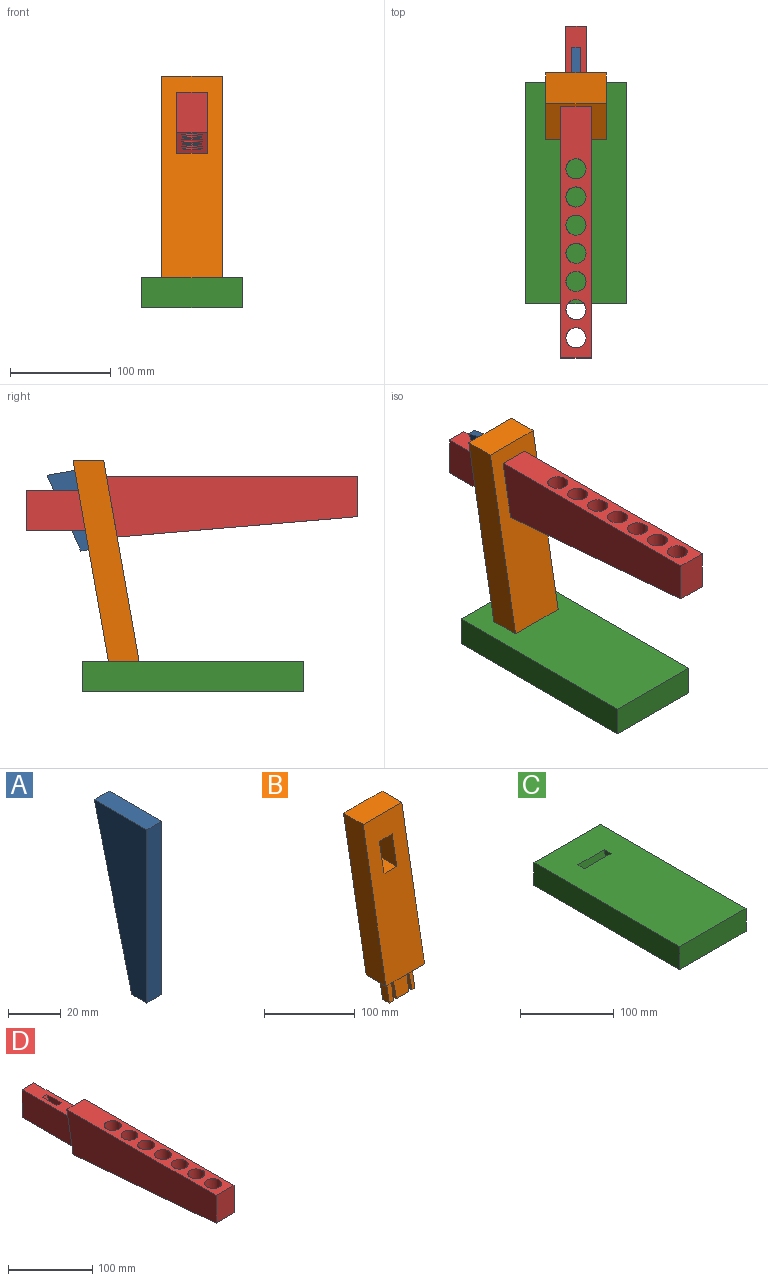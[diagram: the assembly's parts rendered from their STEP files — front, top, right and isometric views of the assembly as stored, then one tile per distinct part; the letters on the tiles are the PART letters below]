
ASSEMBLY  parts=4 mates=3
PART A: 6 faces, bbox 8x28x80 mm
  f0: plane 28x8mm, normal (0,0,1), area 224mm2, adj f1,f3,f4,f5
  f1: plane 80x8mm, normal (0,-1,0), area 640mm2, adj f0,f2,f4,f5
  f2: plane 8x8mm, normal (0,0,-1), area 64mm2, adj f1,f3,f4,f5
  f3: plane 80x20mm, normal (0,0.97,-0.24), area 659.7mm2, adj f0,f2,f4,f5
  f4: plane 80x28mm, normal (-1,0,0), area 1440mm2, adj f0,f1,f2,f3
  f5: plane 80x28mm, normal (1,0,0), area 1440mm2, adj f0,f1,f2,f3
PART B: 25 faces, bbox 60x65.7x230 mm
  f0: plane 30x8mm, normal (0,-0.98,0.17), area 220.9mm2, adj f8,f11,f20,f24
  f1: plane 30x22mm, normal (0,-0.98,0.17), area 624.5mm2, adj f3,f11,f22,f23
  f2: plane 30x6mm, normal (0,-0.98,0.17), area 159.9mm2, adj f4,f11,f19,f21
  f3: plane 19x10.15mm, normal (0,0,-1), area 192.9mm2, adj f1,f6,f22,f23
  f4: plane 10.15x4.5mm, normal (0,0,-1), area 45.7mm2, adj f2,f7,f19,f21
  f5: plane 30x8mm, normal (0,0.98,-0.17), area 220.9mm2, adj f8,f11,f20,f24
  f6: plane 30x22mm, normal (0,0.98,-0.17), area 624.5mm2, adj f3,f11,f22,f23
  f7: plane 30x6mm, normal (0,0.98,-0.17), area 159.9mm2, adj f4,f11,f19,f21
  f8: plane 10.15x6.5mm, normal (0,0,-1), area 66mm2, adj f0,f5,f20,f24
  f9: plane 200x65.73mm, normal (1,0,0), area 6092.6mm2, adj f10,f11,f12,f13
  f10: plane 200x60mm, normal (0,-0.98,0.17), area 11372.8mm2, adj f9,f11,f13,f14,f15,f16,f17,f18
  f11: plane 60x30.46mm, normal (0,0,-1), area 1462.2mm2, adj f0,f1,f2,f5,f6,f7,f9,f10
  f12: plane 200x60mm, normal (0,0.98,-0.17), area 11372.8mm2, adj f9,f11,f13,f14,f15,f16,f17,f18
  f13: plane 60x30.46mm, normal (0,0,1), area 1827.8mm2, adj f9,f10,f12,f14
  f14: plane 200x65.73mm, normal (-1,0,0), area 6092.6mm2, adj f10,f11,f12,f13
  f15: plane 30.46x20mm, normal (0,0,1), area 609.3mm2, adj f10,f12,f16,f18
  f16: plane 40x37.52mm, normal (1,0,0), area 1218.5mm2, adj f10,f12,f15,f17
  f17: plane 30.46x20mm, normal (0,0,-1), area 609.3mm2, adj f10,f12,f16,f18
  f18: plane 40x37.52mm, normal (-1,0,0), area 1218.5mm2, adj f10,f12,f15,f17
  f19: plane 30x15.44mm, normal (1,0,0), area 304.6mm2, adj f2,f4,f7,f11
  f20: plane 30x15.44mm, normal (-1,0,0), area 304.6mm2, adj f0,f5,f8,f11
  f21: plane 30x15.44mm, normal (-1,0,-0.05), area 305mm2, adj f2,f4,f7,f11
  f22: plane 30x15.44mm, normal (1,0,-0.05), area 305mm2, adj f1,f3,f6,f11
  f23: plane 30x15.44mm, normal (-1,0,-0.05), area 305mm2, adj f1,f3,f6,f11
  f24: plane 30x15.44mm, normal (1,0,-0.05), area 305mm2, adj f0,f5,f8,f11
PART C: 10 faces, bbox 100x220x30 mm
  f0: plane 100x30mm, normal (0,1,0), area 3000mm2, adj f1,f3,f4,f5
  f1: plane 220x100mm, normal (0,0,1), area 21593.8mm2, adj f0,f2,f4,f5,f6,f7,f8,f9
  f2: plane 100x30mm, normal (0,-1,0), area 3000mm2, adj f1,f3,f4,f5
  f3: plane 220x100mm, normal (0,0,-1), area 21593.8mm2, adj f0,f2,f4,f5,f6,f7,f8,f9
  f4: plane 220x30mm, normal (-1,0,0), area 6600mm2, adj f0,f1,f2,f3
  f5: plane 220x30mm, normal (1,0,0), area 6600mm2, adj f0,f1,f2,f3
  f6: plane 40x30mm, normal (0,-0.98,0.17), area 1218.5mm2, adj f1,f3,f7,f9
  f7: plane 30x15.44mm, normal (-1,0,0), area 304.6mm2, adj f1,f3,f6,f8
  f8: plane 40x30mm, normal (0,0.98,-0.17), area 1218.5mm2, adj f1,f3,f7,f9
  f9: plane 30x15.44mm, normal (1,0,0), area 304.6mm2, adj f1,f3,f6,f8
PART D: 22 faces, bbox 30.4x330.4x60.6 mm
  f0: plane 89.52x20mm, normal (0,0,-1), area 1681.3mm2, adj f1,f6,f9,f10,f18,f19,f20,f21
  f1: plane 40x20mm, normal (0,1,0), area 800mm2, adj f0,f2,f9,f10
  f2: plane 82.47x20mm, normal (0,0,1), area 1453.9mm2, adj f1,f6,f9,f10,f18,f19,f20,f21
  f3: plane 250x30mm, normal (0,0,1), area 5300.9mm2, adj f4,f6,f7,f8,f11,f12,f13,f14
  f4: plane 40x30mm, normal (0,-1,0), area 1200mm2, adj f3,f5,f7,f8
  f5: plane 239.73x30.36mm, normal (0,-0.08,-1), area 4999.8mm2, adj f4,f6,f7,f8,f11,f12,f13,f14
  f6: plane 60.29x30mm, normal (0,0.98,-0.17), area 1024.2mm2, adj f0,f2,f3,f5,f7,f8,f9,f10
  f7: plane 250x60.29mm, normal (1,0,0), area 12323.4mm2, adj f3,f4,f5,f6
  f8: plane 250x60.29mm, normal (-1,0,0), area 12323.4mm2, adj f3,f4,f5,f6
  f9: plane 89.52x40mm, normal (1,0,0), area 3439.8mm2, adj f0,f1,f2,f6
  f10: plane 89.52x40mm, normal (-1,0,0), area 3439.8mm2, adj f0,f1,f2,f6
  f11: cylinder r=10mm len=56.79mm, axis (0,0,1), area 3516.3mm2, adj f3,f5
  f12: cylinder r=10mm len=54.41mm, axis (0,0,1), area 3367.2mm2, adj f3,f5
  f13: cylinder r=10mm len=52.04mm, axis (0,0,1), area 3218mm2, adj f3,f5
  f14: cylinder r=10mm len=49.67mm, axis (0,0,1), area 3068.9mm2, adj f3,f5
  f15: cylinder r=10mm len=47.29mm, axis (0,0,1), area 2919.8mm2, adj f3,f5
  f16: cylinder r=10mm len=44.92mm, axis (0,0,1), area 2770.7mm2, adj f3,f5
  f17: cylinder r=10mm len=42.55mm, axis (0,0,1), area 2621.6mm2, adj f3,f5
  f18: plane 40x8mm, normal (0,0.98,-0.17), area 324.9mm2, adj f0,f2,f20,f21
  f19: plane 40x17.84mm, normal (0,-0.91,0.41), area 350.4mm2, adj f0,f2,f20,f21
  f20: plane 40x31.49mm, normal (1,0,0), area 761.5mm2, adj f0,f2,f18,f19
  f21: plane 40x31.49mm, normal (-1,0,0), area 761.5mm2, adj f0,f2,f18,f19
PLACE A rot(axis=(-1,0,0),10deg) t=(110.76,231.77,246.8)mm
PLACE B t=(136.76,369.12,47.63)mm
PLACE C t=(156.76,190.64,106.91)mm
PLACE D t=(91.76,100.32,66.65)mm
MATE fastened B.f17 <-> D.f2  axis (0,0,1) through (96.76,164.16,276.91)mm
MATE fastened C.f1 <-> B.f11  axis (0,0,1) through (86.76,154.49,106.91)mm
MATE fastened B.f12 <-> A.f1  axis (0,0.98,-0.17) through (106.76,199.91,306.91)mm
